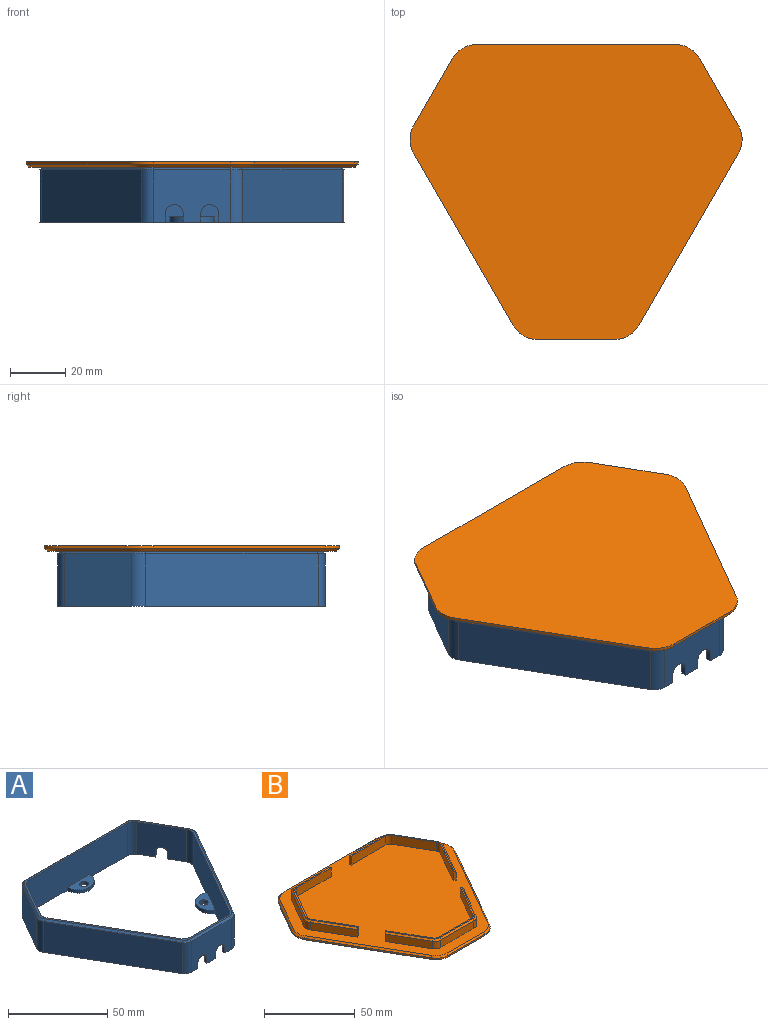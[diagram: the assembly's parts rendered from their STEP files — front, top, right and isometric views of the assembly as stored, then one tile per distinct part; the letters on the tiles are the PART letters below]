
ASSEMBLY  parts=2 mates=1
PART A: 58 faces, bbox 110.1x96.7x20 mm
  f0: plane 100.79x96.69mm, normal (0,0,-1), area 580.8mm2, adj f1,f3,f4,f6,f7,f8,f9,f10
  f1: plane 22.31x20mm, normal (-0.87,-0.5,0), area 477.5mm2, adj f0,f2,f10,f11,f26,f43,f44,f45
  f2: plane 79.22x45.38mm, normal (0,0,-1), area 277.5mm2, adj f1,f3,f5,f11,f12,f13,f14,f15
  f3: plane 25.76x20mm, normal (0,1,0), area 439.8mm2, adj f0,f2,f12,f25,f26,f27,f37,f38
  f4: plane 60.38x34.86mm, normal (0.87,0.5,0), area 1362.5mm2, adj f0,f7,f25,f26,f34,f36
  f5: plane 60.38x34.86mm, normal (-0.87,0.5,0), area 1362.5mm2, adj f2,f11,f12,f26,f31,f33
  f6: plane 69.73x20mm, normal (0,-1,0), area 1362.5mm2, adj f0,f9,f10,f26,f28,f30
  f7: cylinder r=5mm len=20mm, axis (0,0,-1), area 104.7mm2, adj f0,f4,f8,f26
  f8: plane 22.31x20mm, normal (0.87,-0.5,0), area 515.2mm2, adj f0,f7,f9,f26
  f9: cylinder r=5mm len=20mm, axis (0,0,-1), area 104.7mm2, adj f0,f6,f8,f26
  f10: cylinder r=5mm len=20mm, axis (0,0,-1), area 104.7mm2, adj f0,f1,f6,f26
  f11: cylinder r=5mm len=20mm, axis (0,0,-1), area 104.7mm2, adj f1,f2,f5,f26
  f12: cylinder r=5mm len=20mm, axis (0,0,-1), area 104.7mm2, adj f2,f3,f5,f26
  f13: plane 62.38x36.02mm, normal (0.87,-0.5,0), area 1368.7mm2, adj f2,f14,f24,f54
  f14: cylinder r=5mm len=19mm, axis (0,0,-1), area 99.5mm2, adj f2,f13,f15,f56
  f15: plane 24.31x19mm, normal (0.87,0.5,0), area 495.6mm2, adj f0,f2,f14,f16,f43,f44,f45,f57
  f16: cylinder r=5mm len=19mm, axis (0,0,-1), area 99.5mm2, adj f0,f15,f17,f55
  f17: plane 72.03x19mm, normal (0,1,0), area 1368.7mm2, adj f0,f16,f18,f53
  f18: cylinder r=5mm len=19mm, axis (0,0,-1), area 99.5mm2, adj f0,f17,f19,f51
  f19: plane 24.31x19mm, normal (-0.87,0.5,0), area 533.3mm2, adj f0,f18,f20,f49
  f20: cylinder r=5mm len=19mm, axis (0,0,-1), area 99.5mm2, adj f0,f19,f21,f47
  f21: plane 62.38x36.02mm, normal (-0.87,-0.5,0), area 1368.7mm2, adj f0,f20,f22,f46
  f22: cylinder r=5mm len=19mm, axis (0,0,-1), area 99.5mm2, adj f0,f21,f23,f48
  f23: plane 28.07x19mm, normal (0,-1,0), area 457.9mm2, adj f0,f2,f22,f24,f27,f37,f38,f39
  f24: cylinder r=5mm len=19mm, axis (0,0,-1), area 99.5mm2, adj f2,f13,f23,f52
  f25: cylinder r=5mm len=20mm, axis (0,0,-1), area 104.7mm2, adj f0,f3,f4,f26
  f26: plane 108.1x94.69mm, normal (0,0,1), area 327.5mm2, adj f1,f3,f4,f5,f6,f7,f8,f9
  f27: plane 6.33x2mm, normal (0,0,-1), area 12.7mm2, adj f3,f23,f37,f42
  f28: cylinder r=8mm len=16mm, axis (0,0,-1), area 50.3mm2, adj f0,f6,f30
  f29: cylinder r=2.25mm len=4.5mm, axis (0,0,-1), area 28.3mm2, adj f0,f30
  f30: plane 16x8mm, normal (0,0,1), area 84.6mm2, adj f6,f28,f29
  f31: cylinder r=8mm len=14.93mm, axis (0,0,-1), area 50.3mm2, adj f2,f5,f33
  f32: cylinder r=2.25mm len=4.5mm, axis (0,0,-1), area 28.3mm2, adj f2,f33
  f33: plane 14.93x12mm, normal (0,0,1), area 84.6mm2, adj f5,f31,f32
  f34: cylinder r=8mm len=14.93mm, axis (0,0,-1), area 50.3mm2, adj f0,f4,f36
  f35: cylinder r=2.25mm len=4.5mm, axis (0,0,-1), area 28.3mm2, adj f0,f36
  f36: plane 14.93x12mm, normal (0,0,1), area 84.6mm2, adj f4,f34,f35
  f37: plane 3.25x2mm, normal (-1,0,0), area 6.5mm2, adj f3,f23,f27,f38
  f38: cylinder r=3.25mm len=6.5mm, axis (0,-1,0), area 20.4mm2, adj f3,f23,f37,f39
  f39: plane 3.25x2mm, normal (1,0,0), area 6.5mm2, adj f0,f3,f23,f38
  f40: plane 3.25x2mm, normal (-1,0,0), area 6.5mm2, adj f2,f3,f23,f41
  f41: cylinder r=3.25mm len=6.5mm, axis (0,-1,0), area 20.4mm2, adj f3,f23,f40,f42
  f42: plane 3.25x2mm, normal (1,0,0), area 6.5mm2, adj f3,f23,f27,f41
  f43: plane 3.25x1.73mm, normal (0.5,-0.87,0), area 6.5mm2, adj f0,f1,f15,f44
  f44: cylinder r=3.25mm len=6.63mm, axis (0.87,0.5,0), area 20.4mm2, adj f1,f15,f43,f45
  f45: plane 3.25x1.73mm, normal (-0.5,0.87,0), area 6.5mm2, adj f1,f2,f15,f44
  f46: plane 62.88x36.88mm, normal (-0.61,-0.35,0.71), area 101.9mm2, adj f21,f26,f47,f48
  f47: cone r=4mm half-angle=45deg, axis (0,0,-1), area 6.7mm2, adj f20,f26,f46,f49
  f48: cone r=4mm half-angle=45deg, axis (0,0,-1), area 6.7mm2, adj f22,f26,f46,f50
  f49: plane 24.81x14.9mm, normal (-0.61,0.35,0.71), area 39.7mm2, adj f19,f26,f47,f51
  f50: plane 28.07x1mm, normal (0,-0.71,0.71), area 39.7mm2, adj f23,f26,f48,f52
  f51: cone r=4mm half-angle=45deg, axis (0,0,-1), area 6.7mm2, adj f18,f26,f49,f53
  f52: cone r=4mm half-angle=45deg, axis (0,0,-1), area 6.7mm2, adj f24,f26,f50,f54
  f53: plane 72.03x1mm, normal (0,0.71,0.71), area 101.9mm2, adj f17,f26,f51,f55
  f54: plane 62.88x36.88mm, normal (0.61,-0.35,0.71), area 101.9mm2, adj f13,f26,f52,f56
  f55: cone r=4mm half-angle=45deg, axis (0,0,-1), area 6.7mm2, adj f16,f26,f53,f57
  f56: cone r=4mm half-angle=45deg, axis (0,0,-1), area 6.7mm2, adj f14,f26,f54,f57
  f57: plane 24.81x14.9mm, normal (0.61,0.35,0.71), area 39.7mm2, adj f15,f26,f55,f56
PART B: 80 faces, bbox 120.1x106.7x8 mm
  f0: plane 118.1x104.69mm, normal (0,0,1), area 8573mm2, adj f14,f15,f16,f17,f18,f19,f20,f21
  f1: plane 62.38x36.02mm, normal (-0.87,-0.5,0), area 72mm2, adj f2,f12,f13,f53
  f2: cylinder r=10mm len=8.66mm, axis (0,0,-1), area 10.5mm2, adj f1,f3,f13,f55
  f3: plane 28.07x1mm, normal (0,-1,0), area 28.1mm2, adj f2,f4,f13,f57
  f4: cylinder r=10mm len=8.66mm, axis (0,0,-1), area 10.5mm2, adj f3,f5,f13,f59
  f5: plane 62.38x36.02mm, normal (0.87,-0.5,0), area 72mm2, adj f4,f6,f13,f61
  f6: cylinder r=10mm len=10mm, axis (0,0,-1), area 10.5mm2, adj f5,f7,f13,f63
  f7: plane 24.31x14.03mm, normal (0.87,0.5,0), area 28.1mm2, adj f6,f8,f13,f64
  f8: cylinder r=10mm len=8.66mm, axis (0,0,-1), area 10.5mm2, adj f7,f9,f13,f62
  f9: plane 72.03x1mm, normal (0,1,0), area 72mm2, adj f8,f10,f13,f60
  f10: cylinder r=10mm len=8.66mm, axis (0,0,-1), area 10.5mm2, adj f9,f11,f13,f58
  f11: plane 24.31x14.03mm, normal (-0.87,0.5,0), area 28.1mm2, adj f10,f12,f13,f56
  f12: cylinder r=10mm len=10mm, axis (0,0,-1), area 10.5mm2, adj f1,f11,f13,f54
  f13: plane 120.1x106.69mm, normal (0,0,-1), area 9407.3mm2, adj f1,f2,f3,f4,f5,f6,f7,f8
  f14: plane 26.87x5mm, normal (0,1,0), area 134.3mm2, adj f0,f15,f25,f70
  f15: cylinder r=8mm len=6mm, axis (0,0,-1), area 10.4mm2, adj f0,f14,f16,f26,f70
  f16: plane 27.12x6mm, normal (0,-1,0), area 162.7mm2, adj f0,f15,f17,f26
  f17: cylinder r=3mm len=6mm, axis (0,0,-1), area 18.8mm2, adj f0,f16,f18,f26
  f18: plane 22.31x12.88mm, normal (-0.87,-0.5,0), area 154.6mm2, adj f0,f17,f19,f26
  f19: cylinder r=3mm len=6mm, axis (0,0,-1), area 18.8mm2, adj f0,f18,f20,f26
  f20: plane 23.48x13.56mm, normal (-0.87,0.5,0), area 162.7mm2, adj f0,f19,f21,f26
  f21: cylinder r=8mm len=6mm, axis (0,0,-1), area 10.4mm2, adj f0,f20,f22,f26,f74
  f22: plane 23.27x13.43mm, normal (0.87,-0.5,0), area 134.3mm2, adj f0,f21,f23,f74
  f23: cylinder r=4.8mm len=5mm, axis (0,0,-1), area 25.1mm2, adj f0,f22,f24,f73
  f24: plane 22.31x12.88mm, normal (0.87,0.5,0), area 128.8mm2, adj f0,f23,f25,f72
  f25: cylinder r=4.8mm len=5mm, axis (0,0,-1), area 25.1mm2, adj f0,f14,f24,f71
  f26: plane 51.35x43.8mm, normal (0,0,1), area 69.5mm2, adj f15,f16,f17,f18,f19,f20,f21,f70
  f27: plane 26.87x5mm, normal (0,1,0), area 134.3mm2, adj f0,f28,f38,f75
  f28: cylinder r=4.8mm len=5mm, axis (0,0,-1), area 25.1mm2, adj f0,f27,f29,f76
  f29: plane 22.31x12.88mm, normal (-0.87,0.5,0), area 128.8mm2, adj f0,f28,f30,f77
  f30: cylinder r=4.8mm len=5mm, axis (0,0,-1), area 25.1mm2, adj f0,f29,f31,f78
  f31: plane 23.27x13.43mm, normal (-0.87,-0.5,0), area 134.3mm2, adj f0,f30,f32,f79
  f32: cylinder r=8mm len=6mm, axis (0,0,-1), area 10.4mm2, adj f0,f31,f33,f39,f79
  f33: plane 23.48x13.56mm, normal (0.87,0.5,0), area 162.7mm2, adj f0,f32,f34,f39
  f34: cylinder r=3mm len=6mm, axis (0,0,-1), area 18.8mm2, adj f0,f33,f35,f39
  f35: plane 22.31x12.88mm, normal (0.87,-0.5,0), area 154.6mm2, adj f0,f34,f36,f39
  f36: cylinder r=3mm len=6mm, axis (0,0,-1), area 18.8mm2, adj f0,f35,f37,f39
  f37: plane 27.12x6mm, normal (0,-1,0), area 162.7mm2, adj f0,f36,f38,f39
  f38: cylinder r=8mm len=6mm, axis (0,0,-1), area 10.4mm2, adj f0,f27,f37,f39,f75
  f39: plane 51.35x43.8mm, normal (0,0,1), area 69.5mm2, adj f32,f33,f34,f35,f36,f37,f38,f75
  f40: plane 23.27x13.43mm, normal (-0.87,-0.5,0), area 134.3mm2, adj f0,f41,f51,f69
  f41: cylinder r=4.8mm len=5mm, axis (0,0,-1), area 25.1mm2, adj f0,f40,f42,f68
  f42: plane 25.76x5mm, normal (0,-1,0), area 128.8mm2, adj f0,f41,f43,f67
  f43: cylinder r=4.8mm len=5mm, axis (0,0,-1), area 25.1mm2, adj f0,f42,f44,f66
  f44: plane 23.27x13.43mm, normal (0.87,-0.5,0), area 134.3mm2, adj f0,f43,f45,f65
  f45: cylinder r=8mm len=6mm, axis (0,0,-1), area 10.4mm2, adj f0,f44,f46,f52,f65
  f46: plane 23.48x13.56mm, normal (-0.87,0.5,0), area 162.7mm2, adj f0,f45,f47,f52
  f47: cylinder r=3mm len=6mm, axis (0,0,-1), area 18.8mm2, adj f0,f46,f48,f52
  f48: plane 25.76x6mm, normal (0,1,0), area 154.6mm2, adj f0,f47,f49,f52
  f49: cylinder r=3mm len=6mm, axis (0,0,-1), area 18.8mm2, adj f0,f48,f50,f52
  f50: plane 23.48x13.56mm, normal (0.87,0.5,0), area 162.7mm2, adj f0,f49,f51,f52
  f51: cylinder r=8mm len=6mm, axis (0,0,-1), area 10.4mm2, adj f0,f40,f50,f52,f69
  f52: plane 59.29x25.78mm, normal (0,0,1), area 69.5mm2, adj f45,f46,f47,f48,f49,f50,f51,f65
  f53: plane 62.88x36.88mm, normal (-0.61,-0.35,0.71), area 101.9mm2, adj f0,f1,f54,f55
  f54: cone r=9mm half-angle=45deg, axis (0,0,-1), area 14.1mm2, adj f0,f12,f53,f56
  f55: cone r=9mm half-angle=45deg, axis (0,0,-1), area 14.1mm2, adj f0,f2,f53,f57
  f56: plane 24.81x14.9mm, normal (-0.61,0.35,0.71), area 39.7mm2, adj f0,f11,f54,f58
  f57: plane 28.07x1mm, normal (0,-0.71,0.71), area 39.7mm2, adj f0,f3,f55,f59
  f58: cone r=9mm half-angle=45deg, axis (0,0,-1), area 14.1mm2, adj f0,f10,f56,f60
  f59: cone r=9mm half-angle=45deg, axis (0,0,-1), area 14.1mm2, adj f0,f4,f57,f61
  f60: plane 72.03x1mm, normal (0,0.71,0.71), area 101.9mm2, adj f0,f9,f58,f62
  f61: plane 62.88x36.88mm, normal (0.61,-0.35,0.71), area 101.9mm2, adj f0,f5,f59,f63
  f62: cone r=9mm half-angle=45deg, axis (0,0,-1), area 14.1mm2, adj f0,f8,f60,f64
  f63: cone r=9mm half-angle=45deg, axis (0,0,-1), area 14.1mm2, adj f0,f6,f61,f64
  f64: plane 24.81x14.9mm, normal (0.61,0.35,0.71), area 39.7mm2, adj f0,f7,f62,f63
  f65: plane 23.84x14.3mm, normal (0.61,-0.35,0.71), area 38mm2, adj f44,f45,f52,f66
  f66: cone r=3.8mm half-angle=45deg, axis (0,0,-1), area 6.4mm2, adj f43,f52,f65,f67
  f67: plane 25.76x1mm, normal (0,-0.71,0.71), area 36.4mm2, adj f42,f52,f66,f68
  f68: cone r=3.8mm half-angle=45deg, axis (0,0,-1), area 6.4mm2, adj f41,f52,f67,f69
  f69: plane 23.84x14.3mm, normal (-0.61,-0.35,0.71), area 38mm2, adj f40,f51,f52,f68
  f70: plane 26.96x1mm, normal (0,0.71,0.71), area 38mm2, adj f14,f15,f26,f71
  f71: cone r=3.8mm half-angle=45deg, axis (0,0,-1), area 6.4mm2, adj f25,f26,f70,f72
  f72: plane 22.81x13.75mm, normal (0.61,0.35,0.71), area 36.4mm2, adj f24,f26,f71,f73
  f73: cone r=3.8mm half-angle=45deg, axis (0,0,-1), area 6.4mm2, adj f23,f26,f72,f74
  f74: plane 23.77x14.35mm, normal (0.61,-0.35,0.71), area 38mm2, adj f21,f22,f26,f73
  f75: plane 26.96x1mm, normal (0,0.71,0.71), area 38mm2, adj f27,f38,f39,f76
  f76: cone r=3.8mm half-angle=45deg, axis (0,0,-1), area 6.4mm2, adj f28,f39,f75,f77
  f77: plane 22.81x13.75mm, normal (-0.61,0.35,0.71), area 36.4mm2, adj f29,f39,f76,f78
  f78: cone r=3.8mm half-angle=45deg, axis (0,0,-1), area 6.4mm2, adj f30,f39,f77,f79
  f79: plane 23.77x14.35mm, normal (-0.61,-0.35,0.71), area 38mm2, adj f31,f32,f39,f78
PLACE A t=(3.23,22.2,28.51)mm
PLACE B rot(axis=(0,1,0),180deg) t=(3.23,22,50.51)mm
MATE fastened B.f0 <-> A.f26  axis (0,0,-1) through (3.23,-30.49,48.51)mm
